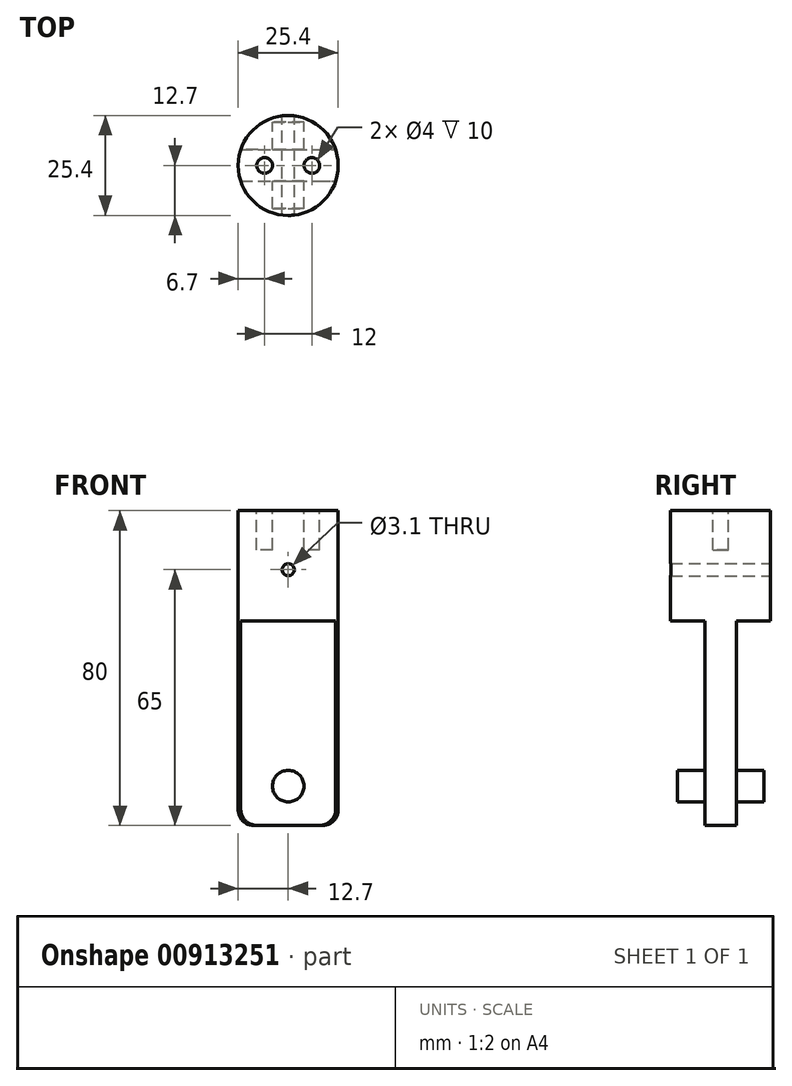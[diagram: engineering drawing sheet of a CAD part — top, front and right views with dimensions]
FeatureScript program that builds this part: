
annotation { "Feature Type Name" : "Feature", "Feature Type Description" : "" }
export const myFeature = defineFeature(function(context is Context, id is Id, definition is map)
    precondition{}
    {
        {
            var Q0;
            Q0=qCreatedBy(makeId("Front.planeOp"),FACE);
            var sketch = newSketch(context, id + "F0", { "sketchPlane" : qUnion([Q0])});
            skCircle(sketch, "E0", {"center": v(0, 0) * mm, "radius": 4 * mm, "construction": true});
            skLineSegment(sketch, "E1.bottom", {"start": v(0, 70) * mm, "end": v(-12.7, 70) * mm});
            skLineSegment(sketch, "E1.top", {"start": v(0, -10) * mm, "end": v(-12.7, -10) * mm});
            skLineSegment(sketch, "E1.left", {"start": v(0, 70) * mm, "end": v(0, -10) * mm});
            skLineSegment(sketch, "E1.right", {"start": v(-12.7, 70) * mm, "end": v(-12.7, -10) * mm});
            skSolve(sketch);
        }
        {
            var Q0;
            Q0=makeQuery(id+"F0.imprint","IMPRINT",FACE,{"disambiguationData":[TD([[makeQuery(id+"F0.imprint","IMPRINT",EDGE,{"derivedFrom":sQuery(id+"F0.wireOp",EDGE,"E1.bottom")}),1.0]])]});
            var Q1;
            Q1=sQuery(id+"F0.wireOp",EDGE,"E1.left");
            revolve(context, id + "F1", {"surfaceOperationType" : NewSurfaceOperationType.NEW, "entities" : qUnion([Q0]), "axis" : qUnion([Q1]), "revolveType" : RevolveType.FULL});
        }
        {
            var Q0;
            Q0=qCreatedBy(makeId("Right.planeOp"),FACE);
            var sketch = newSketch(context, id + "F2", { "sketchPlane" : qUnion([Q0])});
            skPoint(sketch, "E2.0", {"position": v(0, -10) * mm});
            skLineSegment(sketch, "E3.bottom", {"start": v(-4, 42) * mm, "end": v(4, 42) * mm, "construction": true});
            skLineSegment(sketch, "E3.top", {"start": v(-4, -10) * mm, "end": v(4, -10) * mm, "construction": true});
            skLineSegment(sketch, "E3.left", {"start": v(-4, 42) * mm, "end": v(-4, -10) * mm});
            skLineSegment(sketch, "E3.right", {"start": v(4, 42) * mm, "end": v(4, -10) * mm});
            skLineSegment(sketch, "E4.bottom", {"start": v(4, 42) * mm, "end": v(40.23, 42) * mm});
            skLineSegment(sketch, "E4.top", {"start": v(4, -16.87) * mm, "end": v(40.23, -16.87) * mm});
            skLineSegment(sketch, "E4.left", {"start": v(4, 42) * mm, "end": v(4, -16.87) * mm});
            skLineSegment(sketch, "E4.right", {"start": v(40.23, 42) * mm, "end": v(40.23, -16.87) * mm});
            skLineSegment(sketch, "E5.bottom", {"start": v(-4, 42) * mm, "end": v(-29.74, 42) * mm});
            skLineSegment(sketch, "E5.top", {"start": v(-4, -22.23) * mm, "end": v(-29.74, -22.23) * mm});
            skLineSegment(sketch, "E5.left", {"start": v(-4, 42) * mm, "end": v(-4, -22.23) * mm});
            skLineSegment(sketch, "E5.right", {"start": v(-29.74, 42) * mm, "end": v(-29.74, -22.23) * mm});
            skSolve(sketch);
        }
        {
            var Q0;
            Q0 = qSketchRegion(id + "F2", true);
            extrude(context, id + "F3", {"entities" : qUnion([Q0]), "operationType" : NewBodyOperationType.REMOVE, "endBound" : BoundingType.THROUGH_ALL, "oppositeDirection" : true, "depth" : 25 * mm, "offsetDistance" : 25 * mm, "hasSecondDirection" : true, "secondDirectionBound" : SecondDirectionBoundingType.THROUGH_ALL, "secondDirectionOppositeDirection" : false, "secondDirectionDepth" : 25 * mm});
        }
        {
            var Q0;
            Q0=qCreatedBy(makeId("Front.planeOp"),FACE);
            var sketch = newSketch(context, id + "F4", { "sketchPlane" : qUnion([Q0])});
            skCircle(sketch, "E6.0", {"center": v(0, 0) * mm, "radius": 4 * mm});
            skSolve(sketch);
        }
        {
            var Q0;
            Q0 = qSketchRegion(id + "F4", true);
            extrude(context, id + "F5", {"entities" : qUnion([Q0]), "operationType" : NewBodyOperationType.ADD, "endBound" : BoundingType.SYMMETRIC, "depth" : 22 * mm, "offsetDistance" : 25 * mm});
        }
        {
            var Q0;
            Q0=makeQuery(id+"F1.opRevolve","SWEPT_FACE",FACE,{"disambiguationData":[OSD([sQuery(id+"F0.wireOp",EDGE,"E1.bottom")])]});
            var sketch = newSketch(context, id + "F6", { "sketchPlane" : qUnion([Q0])});
            skCircle(sketch, "E7", {"center": v(-6, 0) * mm, "radius": 2 * mm});
            skLineSegment(sketch, "E8", {"start": v(0, 0) * mm, "end": v(0, 3.84) * mm});
            skCircle(sketch, "E9.MirrorC", {"center": v(6, 0) * mm, "radius": 2 * mm});
            skSolve(sketch);
        }
        {
            var Q0;
            Q0 = qSketchRegion(id + "F6", true);
            extrude(context, id + "F7", {"entities" : qUnion([Q0]), "operationType" : NewBodyOperationType.REMOVE, "oppositeDirection" : true, "depth" : 10 * mm, "offsetDistance" : 25 * mm});
        }
        {
            var Q0;
            Q0=makeQuery(id+"F3.boolean.opBoolean","INTERSECT",EDGE,{"disambiguationData":[OD(0.0)],"derivedFrom":[makeQuery(id+"F1.opRevolve","SWEPT_FACE",FACE,{"disambiguationData":[OSD([sQuery(id+"F0.wireOp",EDGE,"E1.right")])]}),makeQuery(id+"F3.opExtrude","SWEPT_FACE",FACE,{"disambiguationData":[OSD([sQuery(id+"F2.wireOp",EDGE,"E3.bottom")])]})]});
            var Q1;
            Q1=makeQuery(id+"F3.boolean.opBoolean","INTERSECT",EDGE,{"disambiguationData":[OD(1.0)],"derivedFrom":[makeQuery(id+"F1.opRevolve","SWEPT_FACE",FACE,{"disambiguationData":[OSD([sQuery(id+"F0.wireOp",EDGE,"E1.right")])]}),makeQuery(id+"F3.opExtrude","SWEPT_FACE",FACE,{"disambiguationData":[OSD([sQuery(id+"F2.wireOp",EDGE,"E3.bottom")])]})]});
            var Q2;
            {var subQ0=sQuery(id+"F0.wireOp",EDGE,"E1.top");var subQ1=sQuery(id+"F0.wireOp",EDGE,"E1.right");Q2=makeQuery(id+"F3.boolean.opBoolean","SPLIT",EDGE,{"disambiguationData":[TD([makeQuery(id+"F3.opExtrude","SWEPT_FACE",FACE,{"disambiguationData":[OSD([sQuery(id+"F2.wireOp",EDGE,"E3.left")])]})])],"derivedFrom":makeQuery(id+"F1.opRevolve","SWEPT_EDGE",EDGE,{"disambiguationData":[OSD([subQ0,subQ1])]})});}
            var Q3;
            {var subQ0=sQuery(id+"F0.wireOp",EDGE,"E1.top");var subQ1=sQuery(id+"F0.wireOp",EDGE,"E1.right");Q3=makeQuery(id+"F3.boolean.opBoolean","SPLIT",EDGE,{"disambiguationData":[TD([makeQuery(id+"F3.opExtrude","SWEPT_FACE",FACE,{"disambiguationData":[OSD([sQuery(id+"F2.wireOp",EDGE,"E3.right")])]})])],"derivedFrom":makeQuery(id+"F1.opRevolve","SWEPT_EDGE",EDGE,{"disambiguationData":[OSD([subQ0,subQ1])]})});}
            fillet(context, id + "F8", {"entities" : qUnion([Q0, Q1, Q2, Q3]), "radius" : 4 * mm, "tangentPropagation" : true, "allowEdgeOverflow" : false});
        }
        {
            var Q0;
            Q0=qCreatedBy(makeId("Front.planeOp"),FACE);
            var sketch = newSketch(context, id + "F9", { "sketchPlane" : qUnion([Q0])});
            skLineSegment(sketch, "E10.0", {"start": v(-12.7, 70) * mm, "end": v(12.7, 70) * mm, "construction": true});
            skLineSegment(sketch, "E11", {"start": v(0, 70) * mm, "end": v(0, 55) * mm, "construction": true});
            skCircle(sketch, "E12", {"center": v(0, 55) * mm, "radius": 1.55 * mm});
            skSolve(sketch);
        }
        {
            var Q0;
            Q0 = qSketchRegion(id + "F9", true);
            extrude(context, id + "F10", {"entities" : qUnion([Q0]), "operationType" : NewBodyOperationType.REMOVE, "endBound" : BoundingType.THROUGH_ALL, "depth" : 30 * mm, "offsetDistance" : 25 * mm, "hasSecondDirection" : true, "secondDirectionBound" : SecondDirectionBoundingType.THROUGH_ALL, "secondDirectionOppositeDirection" : true, "secondDirectionDepth" : 25 * mm});
        }
    });
